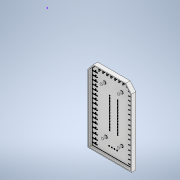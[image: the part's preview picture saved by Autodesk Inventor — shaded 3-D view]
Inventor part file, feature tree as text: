
AUTODESK INVENTOR PART (.ipt)
format: ipt  version: 2021 (Build 250183000, 183)  size: 203,264 bytes
history: native  units: in
note: dims shown in document units (in); Inventor stores cm internally (conversion verified against a paired STEP export)
features: sketch x3, extrude x2, projected_geometry x1
ambient origin geometry x8: Origin, YZ Plane, XZ Plane, XY Plane, X Axis, Y Axis, Z Axis, Center Point
bodies: Solid1 (feature_tree)
feature tree (6):
  sketch  "Sketch1"  dims[d528=0.01in d532=0.01in]
  extrude  "Extrusion1"  Depth=0.01in
  extrude  "Extrusion3"  Depth=0.25in TaperAngle=0.0deg
  sketch  "Sketch2"  dims[d533=0.0625in d534=0.25in d535=0.0in]
  sketch  "Sketch4"  dims[d538=0.08in d539=0.0in]
  projected_geometry  "Projected Loop2"
